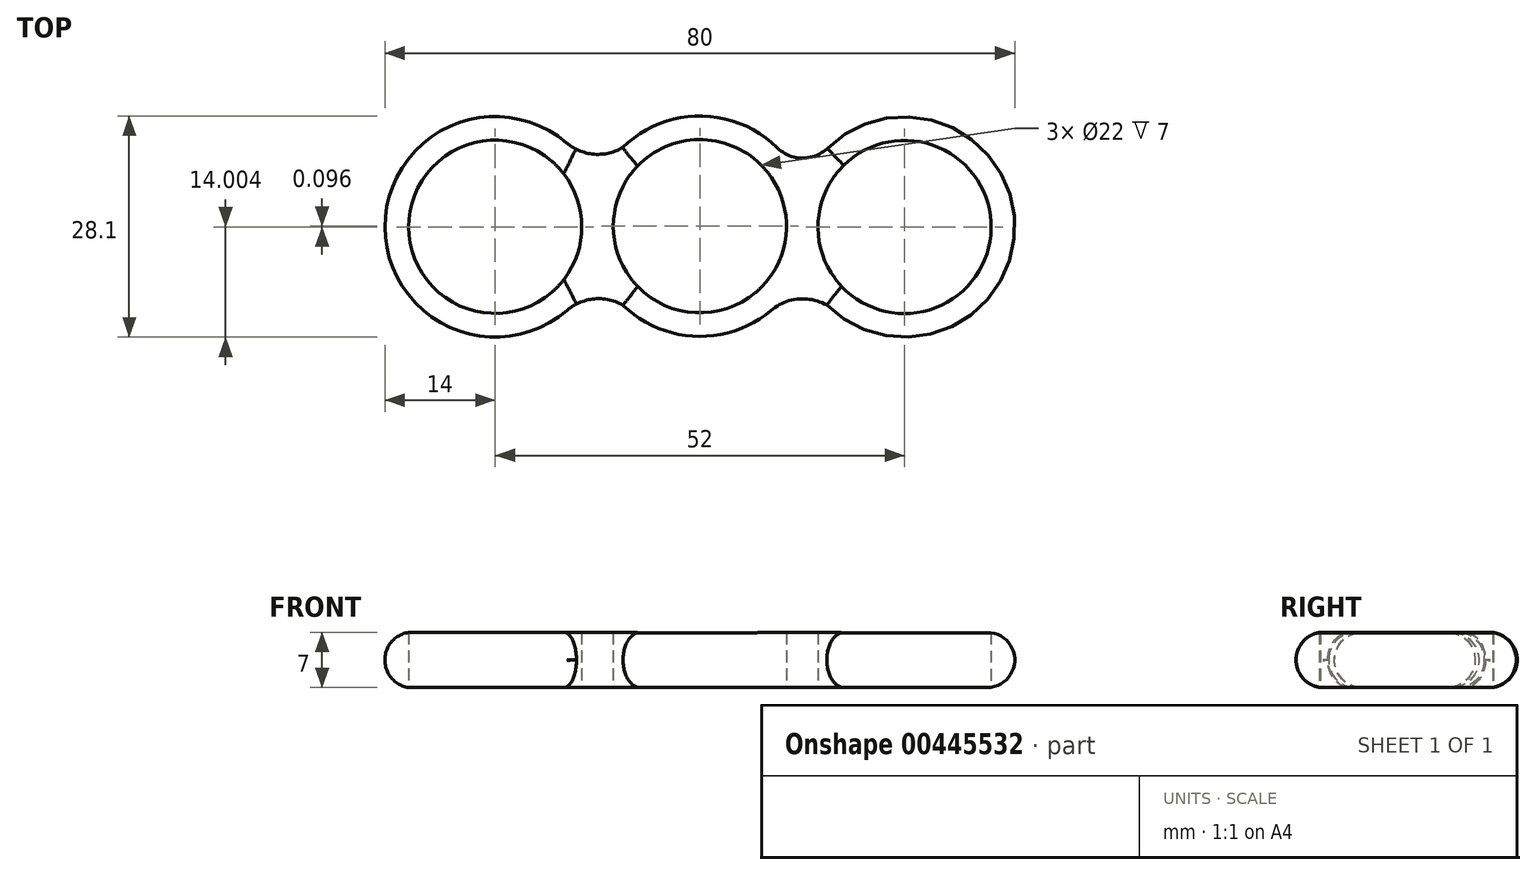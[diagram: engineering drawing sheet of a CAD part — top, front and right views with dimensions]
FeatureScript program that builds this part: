
annotation { "Feature Type Name" : "Feature", "Feature Type Description" : "" }
export const myFeature = defineFeature(function(context is Context, id is Id, definition is map)
    precondition{}
    {
        {
            var Q0;
            Q0=qCreatedBy(makeId("Top.planeOp"),FACE);
            var sketch = newSketch(context, id + "F0", { "sketchPlane" : qUnion([Q0])});
            skCircle(sketch, "E0", {"center": v(0, 0) * mm, "radius": 11 * mm});
            skCircle(sketch, "E1", {"center": v(26, -0.1) * mm, "radius": 11 * mm});
            skCircle(sketch, "E2", {"center": v(-26, -0.07) * mm, "radius": 11 * mm});
            skArc(sketch, "E3", {"start": v(16.2, 9.9) * mm, "mid": v(40, -0.15) * mm, "end": v(16.12, -10.01) * mm});
            skArc(sketch, "E4", {"start": v(9.83, 9.97) * mm, "mid": v(0.01, 14) * mm, "end": v(-9.81, 9.99) * mm});
            skArc(sketch, "E5", {"start": v(9.03, -10.7) * mm, "mid": v(-0.49, -14) * mm, "end": v(-9.75, -10.04) * mm});
            skArc(sketch, "E6", {"start": v(-16.93, 10.59) * mm, "mid": v(-40, -0.11) * mm, "end": v(-16.87, -10.68) * mm});
            skPoint(sketch, "E7.startSnap0", {"position": v(0.01, 14) * mm});
            skArc(sketch, "E8", {"start": v(-16.93, 10.59) * mm, "mid": v(-13.47, 9.15) * mm, "end": v(-9.81, 9.99) * mm});
            skArc(sketch, "E9", {"start": v(-16.87, -10.68) * mm, "mid": v(-13.41, -9.22) * mm, "end": v(-9.75, -10.04) * mm});
            skArc(sketch, "E10", {"start": v(9.03, -10.7) * mm, "mid": v(12.47, -9.25) * mm, "end": v(16.12, -10.01) * mm});
            skArc(sketch, "E11", {"start": v(9.83, 9.97) * mm, "mid": v(13, 8.65) * mm, "end": v(16.2, 9.9) * mm});
            skSolve(sketch);
        }
        {
            var Q0;
            Q0=makeQuery(id+"F0.imprint","IMPRINT",FACE,{"disambiguationData":[TD([[makeQuery(id+"F0.imprint","IMPRINT",EDGE,{"derivedFrom":sQuery(id+"F0.wireOp",EDGE,"E0")}),-1.0]])]});
            extrude(context, id + "F1", {"entities" : qUnion([Q0]), "depth" : 7 * mm});
        }
        {
            var Q0;
            Q0=makeQuery(id+"F1.opExtrude","CAP_EDGE",EDGE,{"disambiguationData":[OSD([sQuery(id+"F0.wireOp",EDGE,"E6")])],"isStart":true});
            var Q1;
            Q1=makeQuery(id+"F1.opExtrude","CAP_EDGE",EDGE,{"disambiguationData":[OSD([sQuery(id+"F0.wireOp",EDGE,"E4")])],"isStart":true});
            var Q2;
            Q2=makeQuery(id+"F1.opExtrude","CAP_EDGE",EDGE,{"disambiguationData":[OSD([sQuery(id+"F0.wireOp",EDGE,"E8")])],"isStart":true});
            var Q3;
            Q3=makeQuery(id+"F1.opExtrude","CAP_EDGE",EDGE,{"disambiguationData":[OSD([sQuery(id+"F0.wireOp",EDGE,"E5")])],"isStart":true});
            var Q4;
            Q4=makeQuery(id+"F1.opExtrude","CAP_EDGE",EDGE,{"disambiguationData":[OSD([sQuery(id+"F0.wireOp",EDGE,"E3")])],"isStart":true});
            var Q5;
            Q5=makeQuery(id+"F1.opExtrude","CAP_EDGE",EDGE,{"disambiguationData":[OSD([sQuery(id+"F0.wireOp",EDGE,"E11")])],"isStart":true});
            var Q6;
            Q6=makeQuery(id+"F1.opExtrude","CAP_EDGE",EDGE,{"disambiguationData":[OSD([sQuery(id+"F0.wireOp",EDGE,"E10")])],"isStart":true});
            var Q7;
            Q7=makeQuery(id+"F1.opExtrude","CAP_EDGE",EDGE,{"disambiguationData":[OSD([sQuery(id+"F0.wireOp",EDGE,"E3")])],"isStart":false});
            var Q8;
            Q8=makeQuery(id+"F1.opExtrude","CAP_EDGE",EDGE,{"disambiguationData":[OSD([sQuery(id+"F0.wireOp",EDGE,"E10")])],"isStart":false});
            var Q9;
            Q9=makeQuery(id+"F1.opExtrude","CAP_EDGE",EDGE,{"disambiguationData":[OSD([sQuery(id+"F0.wireOp",EDGE,"E11")])],"isStart":false});
            var Q10;
            Q10=makeQuery(id+"F1.opExtrude","CAP_EDGE",EDGE,{"disambiguationData":[OSD([sQuery(id+"F0.wireOp",EDGE,"E4")])],"isStart":false});
            var Q11;
            Q11=makeQuery(id+"F1.opExtrude","CAP_EDGE",EDGE,{"disambiguationData":[OSD([sQuery(id+"F0.wireOp",EDGE,"E5")])],"isStart":false});
            var Q12;
            Q12=makeQuery(id+"F1.opExtrude","CAP_EDGE",EDGE,{"disambiguationData":[OSD([sQuery(id+"F0.wireOp",EDGE,"E9")])],"isStart":false});
            var Q13;
            Q13=makeQuery(id+"F1.opExtrude","CAP_EDGE",EDGE,{"disambiguationData":[OSD([sQuery(id+"F0.wireOp",EDGE,"E8")])],"isStart":false});
            var Q14;
            Q14=makeQuery(id+"F1.opExtrude","CAP_EDGE",EDGE,{"disambiguationData":[OSD([sQuery(id+"F0.wireOp",EDGE,"E6")])],"isStart":false});
            var Q15;
            Q15=makeQuery(id+"F1.opExtrude","CAP_EDGE",EDGE,{"disambiguationData":[OSD([sQuery(id+"F0.wireOp",EDGE,"E9")])],"isStart":true});
            fillet(context, id + "F2", {"entities" : qUnion([Q0, Q1, Q2, Q3, Q4, Q5, Q6, Q7, Q8, Q9, Q10, Q11, Q12, Q13, Q14, Q15]), "radius" : 3.5 * mm, "allowEdgeOverflow" : false});
        }
    });
